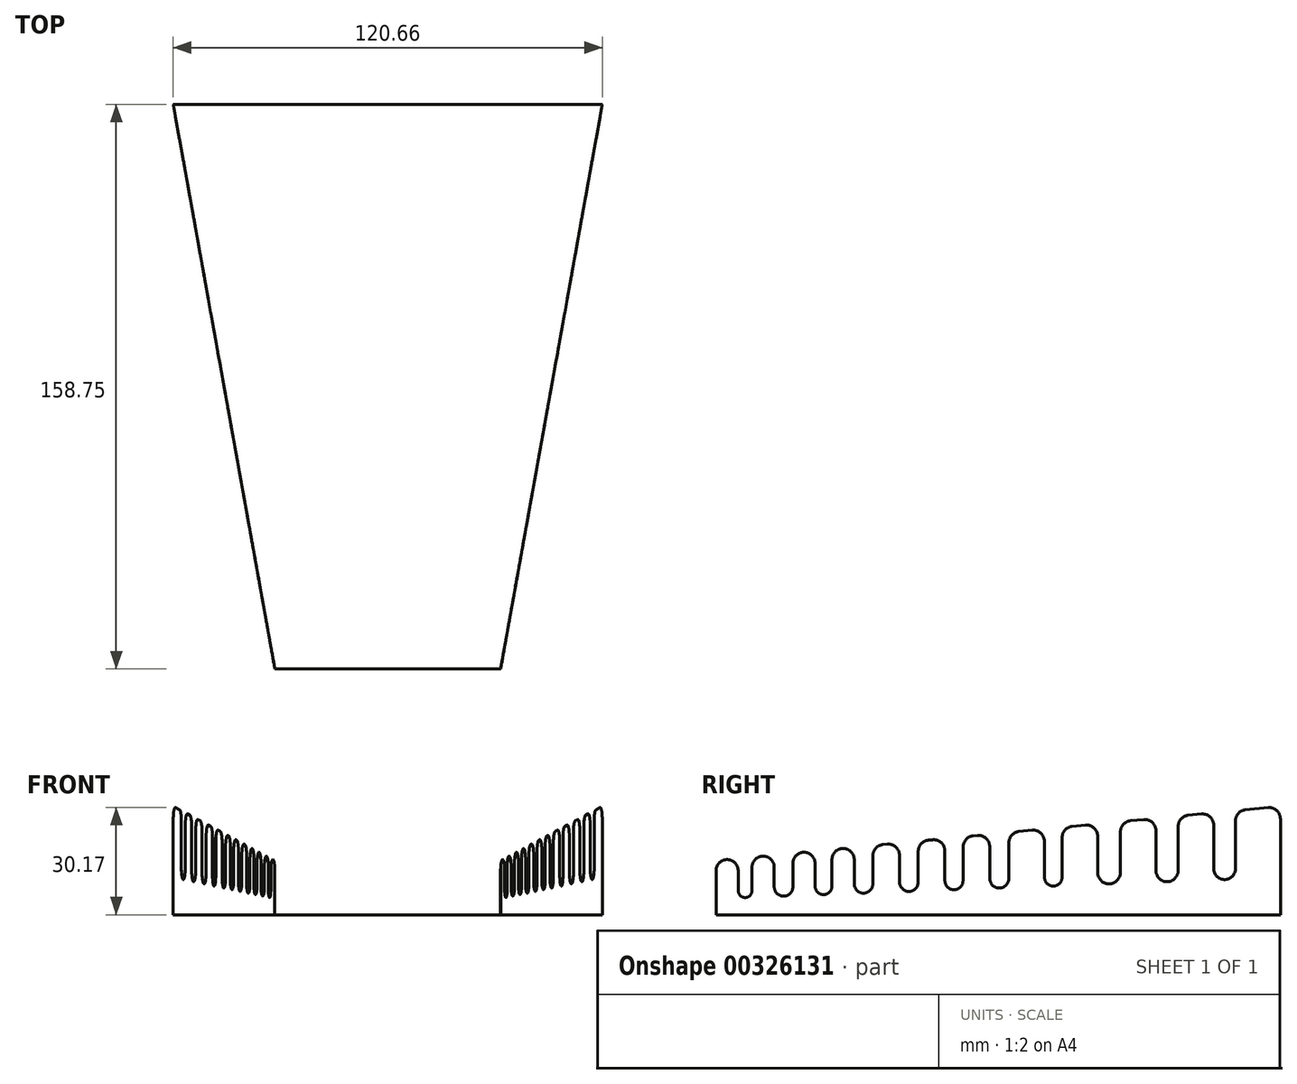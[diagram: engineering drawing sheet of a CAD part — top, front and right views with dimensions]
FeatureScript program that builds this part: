
annotation { "Feature Type Name" : "Feature", "Feature Type Description" : "" }
export const myFeature = defineFeature(function(context is Context, id is Id, definition is map)
    precondition{}
    {
        {
            var Q0;
            Q0=qCreatedBy(makeId("Top.planeOp"),FACE);
            var sketch = newSketch(context, id + "F0", { "sketchPlane" : qUnion([Q0])});
            skLineSegment(sketch, "E0", {"start": v(-31.75, 0) * mm, "end": v(31.75, 0) * mm});
            skLineSegment(sketch, "E1", {"start": v(31.75, 0) * mm, "end": v(60.32, 158.75) * mm});
            skLineSegment(sketch, "E2", {"start": v(60.33, 158.75) * mm, "end": v(-60.33, 158.75) * mm});
            skLineSegment(sketch, "E3", {"start": v(-60.32, 158.75) * mm, "end": v(-31.75, 0) * mm});
            skLineSegment(sketch, "E4", {"start": v(0, 0) * mm, "end": v(0, 306.2) * mm, "construction": true});
            skSolve(sketch);
        }
        {
            var Q0;
            Q0 = qSketchRegion(id + "F0", true);
            extrude(context, id + "F1", {"entities" : qUnion([Q0]), "depth" : 3 / 406.4 * mm});
        }
        {
            var Q0;
            Q0=makeQuery(id+"F1.opExtrude","SWEPT_FACE",FACE,{"disambiguationData":[OSD([sQuery(id+"F0.wireOp",EDGE,"E1")])]});
            var sketch = newSketch(context, id + "F2", { "sketchPlane" : qUnion([Q0])});
            skLineSegment(sketch, "E5", {"start": v(5.62, 0) * mm, "end": v(166.93, 0) * mm});
            skLineSegment(sketch, "E6", {"start": v(166.93, 0) * mm, "end": v(166.93, 27) * mm});
            skLineSegment(sketch, "E7", {"start": v(163.45, 30.15) * mm, "end": v(156.96, 29.54) * mm});
            skLineSegment(sketch, "E8", {"start": v(5.62, 12.35) * mm, "end": v(5.62, 0) * mm});
            skLineSegment(sketch, "E9", {"start": v(104.56, 21.7) * mm, "end": v(104.56, 10.63) * mm});
            skLineSegment(sketch, "E10", {"start": v(99.48, 20.62) * mm, "end": v(99.48, 10.63) * mm});
            skLineSegment(sketch, "E11", {"start": v(89.32, 20.26) * mm, "end": v(89.32, 10.25) * mm});
            skLineSegment(sketch, "E12", {"start": v(83.86, 19.14) * mm, "end": v(83.86, 10.25) * mm});
            skLineSegment(sketch, "E13", {"start": v(76.24, 19.02) * mm, "end": v(76.24, 9.64) * mm});
            skLineSegment(sketch, "E14", {"start": v(71.03, 17.93) * mm, "end": v(71.03, 9.64) * mm});
            skLineSegment(sketch, "E15", {"start": v(63.4, 17.81) * mm, "end": v(63.4, 9.23) * mm});
            skLineSegment(sketch, "E16", {"start": v(58.08, 16.7) * mm, "end": v(58.08, 9.23) * mm});
            skLineSegment(sketch, "E17", {"start": v(38.77, 15.48) * mm, "end": v(38.77, 8.07) * mm});
            skLineSegment(sketch, "E18", {"start": v(33.95, 14.43) * mm, "end": v(33.95, 8.07) * mm});
            skLineSegment(sketch, "E19", {"start": v(27.6, 14.43) * mm, "end": v(27.6, 7.9) * mm});
            skLineSegment(sketch, "E20.trimOffspring", {"start": v(96, 23.78) * mm, "end": v(92.2, 23.42) * mm});
            skLineSegment(sketch, "E21.trimOffspring", {"start": v(80.38, 22.3) * mm, "end": v(79.11, 22.18) * mm});
            skLineSegment(sketch, "E22.trimOffspring", {"start": v(67.56, 21.1) * mm, "end": v(66.29, 20.97) * mm});
            skLineSegment(sketch, "E23.trimOffspring", {"start": v(54.6, 19.87) * mm, "end": v(53.33, 19.75) * mm});
            skLineSegment(sketch, "E24.trimOffspring", {"start": v(30.47, 17.59) * mm, "end": v(30.47, 17.59) * mm});
            skLineSegment(sketch, "E25", {"start": v(22.26, 13.32) * mm, "end": v(22.26, 7.9) * mm});
            skLineSegment(sketch, "E26", {"start": v(15.91, 6.8) * mm, "end": v(15.91, 13.32) * mm});
            skLineSegment(sketch, "E27", {"start": v(11.97, 12.35) * mm, "end": v(11.97, 6.8) * mm});
            skLineSegment(sketch, "E28", {"start": v(45.12, 8.75) * mm, "end": v(45.12, 15.48) * mm});
            skLineSegment(sketch, "E29", {"start": v(50.46, 16.59) * mm, "end": v(50.46, 8.75) * mm});
            skLineSegment(sketch, "E30.trimOffspring", {"start": v(8.5, 15.51) * mm, "end": v(8.5, 15.51) * mm});
            skLineSegment(sketch, "E31.trimOffspring", {"start": v(18.79, 16.48) * mm, "end": v(18.79, 16.48) * mm});
            skLineSegment(sketch, "E32.trimOffspring", {"start": v(41.65, 18.64) * mm, "end": v(41.65, 18.64) * mm});
            skPoint(sketch, "E33.visualSharp", {"position": v(5.62, 15.24) * mm});
            skArc(sketch, "E33.filletArc", {"start": v(8.5, 15.51) * mm, "mid": v(6.45, 14.49) * mm, "end": v(5.62, 12.35) * mm});
            skPoint(sketch, "E34.visualSharp", {"position": v(11.97, 15.84) * mm});
            skArc(sketch, "E34.filletArc", {"start": v(11.97, 12.35) * mm, "mid": v(10.94, 14.7) * mm, "end": v(8.5, 15.51) * mm});
            skPoint(sketch, "E35.visualSharp", {"position": v(15.91, 16.21) * mm});
            skArc(sketch, "E35.filletArc", {"start": v(18.79, 16.48) * mm, "mid": v(16.74, 15.46) * mm, "end": v(15.91, 13.32) * mm});
            skPoint(sketch, "E36.visualSharp", {"position": v(22.26, 16.81) * mm});
            skArc(sketch, "E36.filletArc", {"start": v(22.26, 13.32) * mm, "mid": v(21.22, 15.67) * mm, "end": v(18.79, 16.48) * mm});
            skPoint(sketch, "E37.visualSharp", {"position": v(27.6, 17.32) * mm});
            skArc(sketch, "E37.filletArc", {"start": v(30.47, 17.59) * mm, "mid": v(28.42, 16.56) * mm, "end": v(27.6, 14.43) * mm});
            skPoint(sketch, "E38.visualSharp", {"position": v(33.95, 17.92) * mm});
            skArc(sketch, "E38.filletArc", {"start": v(33.95, 14.43) * mm, "mid": v(32.9, 16.77) * mm, "end": v(30.47, 17.59) * mm});
            skPoint(sketch, "E39.visualSharp", {"position": v(38.77, 18.37) * mm});
            skArc(sketch, "E39.filletArc", {"start": v(41.65, 18.64) * mm, "mid": v(39.6, 17.62) * mm, "end": v(38.77, 15.48) * mm});
            skPoint(sketch, "E40.visualSharp", {"position": v(45.12, 18.97) * mm});
            skArc(sketch, "E40.filletArc", {"start": v(45.12, 15.48) * mm, "mid": v(44.08, 17.83) * mm, "end": v(41.65, 18.64) * mm});
            skPoint(sketch, "E41.visualSharp", {"position": v(50.46, 19.48) * mm});
            skArc(sketch, "E41.filletArc", {"start": v(53.33, 19.75) * mm, "mid": v(51.28, 18.72) * mm, "end": v(50.46, 16.59) * mm});
            skPoint(sketch, "E42.visualSharp", {"position": v(58.08, 20.2) * mm});
            skArc(sketch, "E42.filletArc", {"start": v(58.08, 16.7) * mm, "mid": v(57.04, 19.05) * mm, "end": v(54.6, 19.87) * mm});
            skPoint(sketch, "E43.visualSharp", {"position": v(63.4, 20.7) * mm});
            skArc(sketch, "E43.filletArc", {"start": v(66.29, 20.97) * mm, "mid": v(64.24, 19.95) * mm, "end": v(63.4, 17.81) * mm});
            skPoint(sketch, "E44.visualSharp", {"position": v(71.03, 21.42) * mm});
            skArc(sketch, "E44.filletArc", {"start": v(71.03, 17.93) * mm, "mid": v(70, 20.28) * mm, "end": v(67.56, 21.1) * mm});
            skPoint(sketch, "E45.visualSharp", {"position": v(76.24, 21.91) * mm});
            skArc(sketch, "E45.filletArc", {"start": v(79.11, 22.18) * mm, "mid": v(77.06, 21.16) * mm, "end": v(76.24, 19.02) * mm});
            skPoint(sketch, "E46.visualSharp", {"position": v(83.86, 22.63) * mm});
            skArc(sketch, "E46.filletArc", {"start": v(83.86, 19.14) * mm, "mid": v(82.82, 21.5) * mm, "end": v(80.38, 22.3) * mm});
            skPoint(sketch, "E47.visualSharp", {"position": v(89.32, 23.15) * mm});
            skArc(sketch, "E47.filletArc", {"start": v(92.2, 23.42) * mm, "mid": v(90.14, 22.4) * mm, "end": v(89.32, 20.26) * mm});
            skPoint(sketch, "E48.visualSharp", {"position": v(99.48, 24.1) * mm});
            skArc(sketch, "E48.filletArc", {"start": v(99.48, 20.62) * mm, "mid": v(98.44, 22.97) * mm, "end": v(96, 23.78) * mm});
            skPoint(sketch, "E49.visualSharp", {"position": v(104.56, 24.59) * mm});
            skArc(sketch, "E49.filletArc", {"start": v(107.43, 24.86) * mm, "mid": v(105.38, 23.84) * mm, "end": v(104.56, 21.7) * mm});
            skPoint(sketch, "E50.visualSharp", {"position": v(166.93, 30.48) * mm});
            skArc(sketch, "E50.filletArc", {"start": v(166.93, 27) * mm, "mid": v(165.89, 29.34) * mm, "end": v(163.45, 30.15) * mm});
            skLineSegment(sketch, "E51", {"start": v(14.02, 4.83) * mm, "end": v(151.1, 9.9) * mm, "construction": true});
            skArc(sketch, "E52", {"start": v(11.97, 6.8) * mm, "mid": v(13.94, 4.82) * mm, "end": v(15.91, 6.8) * mm});
            skArc(sketch, "E53", {"start": v(22.26, 7.9) * mm, "mid": v(24.93, 5.23) * mm, "end": v(27.6, 7.9) * mm});
            skArc(sketch, "E54", {"start": v(33.95, 8.07) * mm, "mid": v(36.36, 5.66) * mm, "end": v(38.77, 8.07) * mm});
            skArc(sketch, "E55", {"start": v(45.12, 8.75) * mm, "mid": v(47.79, 6.08) * mm, "end": v(50.46, 8.75) * mm});
            skArc(sketch, "E56", {"start": v(58.08, 9.23) * mm, "mid": v(60.74, 6.56) * mm, "end": v(63.4, 9.23) * mm});
            skArc(sketch, "E57", {"start": v(71.03, 9.64) * mm, "mid": v(73.63, 7.04) * mm, "end": v(76.24, 9.64) * mm});
            skArc(sketch, "E58", {"start": v(83.86, 10.25) * mm, "mid": v(86.59, 7.52) * mm, "end": v(89.32, 10.25) * mm});
            skArc(sketch, "E59", {"start": v(99.48, 10.63) * mm, "mid": v(102.02, 8.09) * mm, "end": v(104.56, 10.63) * mm});
            skLineSegment(sketch, "E60", {"start": v(114.72, 22.06) * mm, "end": v(114.72, 11.92) * mm});
            skLineSegment(sketch, "E61", {"start": v(121.2, 23.27) * mm, "end": v(121.2, 11.92) * mm});
            skLineSegment(sketch, "E62", {"start": v(131.35, 23.63) * mm, "end": v(131.35, 12.47) * mm});
            skLineSegment(sketch, "E63", {"start": v(137.7, 24.83) * mm, "end": v(137.7, 12.47) * mm});
            skLineSegment(sketch, "E64", {"start": v(147.86, 25.19) * mm, "end": v(147.86, 13.02) * mm});
            skLineSegment(sketch, "E65", {"start": v(154.09, 26.38) * mm, "end": v(154.09, 13.02) * mm});
            skArc(sketch, "E66", {"start": v(114.72, 11.92) * mm, "mid": v(117.96, 8.68) * mm, "end": v(121.2, 11.92) * mm});
            skArc(sketch, "E67", {"start": v(131.35, 12.47) * mm, "mid": v(134.53, 9.3) * mm, "end": v(137.7, 12.47) * mm});
            skArc(sketch, "E68", {"start": v(147.86, 13.02) * mm, "mid": v(150.98, 9.9) * mm, "end": v(154.09, 13.02) * mm});
            skLineSegment(sketch, "E69.trimOffspring", {"start": v(144.4, 28.35) * mm, "end": v(140.58, 28) * mm});
            skLineSegment(sketch, "E70.trimOffspring", {"start": v(127.88, 26.8) * mm, "end": v(124.07, 26.43) * mm});
            skLineSegment(sketch, "E71.trimOffspring", {"start": v(111.24, 25.22) * mm, "end": v(107.43, 24.86) * mm});
            skPoint(sketch, "E72.visualSharp", {"position": v(154.09, 29.27) * mm});
            skArc(sketch, "E72.filletArc", {"start": v(156.96, 29.54) * mm, "mid": v(154.91, 28.51) * mm, "end": v(154.09, 26.38) * mm});
            skPoint(sketch, "E73.visualSharp", {"position": v(147.86, 28.68) * mm});
            skArc(sketch, "E73.filletArc", {"start": v(147.86, 25.19) * mm, "mid": v(146.83, 27.54) * mm, "end": v(144.4, 28.35) * mm});
            skPoint(sketch, "E74.visualSharp", {"position": v(137.7, 27.72) * mm});
            skArc(sketch, "E74.filletArc", {"start": v(140.58, 28) * mm, "mid": v(138.53, 26.97) * mm, "end": v(137.7, 24.83) * mm});
            skPoint(sketch, "E75.visualSharp", {"position": v(131.35, 27.12) * mm});
            skArc(sketch, "E75.filletArc", {"start": v(131.35, 23.63) * mm, "mid": v(130.32, 25.98) * mm, "end": v(127.88, 26.8) * mm});
            skPoint(sketch, "E76.visualSharp", {"position": v(121.2, 26.16) * mm});
            skArc(sketch, "E76.filletArc", {"start": v(124.07, 26.43) * mm, "mid": v(122.02, 25.4) * mm, "end": v(121.2, 23.27) * mm});
            skPoint(sketch, "E77.visualSharp", {"position": v(114.72, 25.55) * mm});
            skArc(sketch, "E77.filletArc", {"start": v(114.72, 22.06) * mm, "mid": v(113.68, 24.4) * mm, "end": v(111.24, 25.22) * mm});
            skSolve(sketch);
        }
        {
            var Q0;
            Q0 = qSketchRegion(id + "F2", true);
            extrude(context, id + "F3", {"entities" : qUnion([Q0]), "depth" : 3 / 406.4 * mm});
        }
        {
            var Q0;
            Q0=makeQuery(id+"F3.opExtrude","SWEPT_BODY",BODY,{"disambiguationData":[OSD([sQuery(id+"F2.wireOp",EDGE,"E5"),sQuery(id+"F2.wireOp",EDGE,"E6"),sQuery(id+"F2.wireOp",EDGE,"E7"),sQuery(id+"F2.wireOp",EDGE,"E8"),sQuery(id+"F2.wireOp",EDGE,"E9"),sQuery(id+"F2.wireOp",EDGE,"E10"),sQuery(id+"F2.wireOp",EDGE,"E11"),sQuery(id+"F2.wireOp",EDGE,"E12"),sQuery(id+"F2.wireOp",EDGE,"E13"),sQuery(id+"F2.wireOp",EDGE,"E14"),sQuery(id+"F2.wireOp",EDGE,"E15"),sQuery(id+"F2.wireOp",EDGE,"E16"),sQuery(id+"F2.wireOp",EDGE,"E17"),sQuery(id+"F2.wireOp",EDGE,"E18"),sQuery(id+"F2.wireOp",EDGE,"E19"),sQuery(id+"F2.wireOp",EDGE,"E20.trimOffspring"),sQuery(id+"F2.wireOp",EDGE,"E21.trimOffspring"),sQuery(id+"F2.wireOp",EDGE,"E22.trimOffspring"),sQuery(id+"F2.wireOp",EDGE,"E23.trimOffspring"),sQuery(id+"F2.wireOp",EDGE,"E24.trimOffspring"),sQuery(id+"F2.wireOp",EDGE,"E25"),sQuery(id+"F2.wireOp",EDGE,"E26"),sQuery(id+"F2.wireOp",EDGE,"E27"),sQuery(id+"F2.wireOp",EDGE,"E28"),sQuery(id+"F2.wireOp",EDGE,"E29"),sQuery(id+"F2.wireOp",EDGE,"E30.trimOffspring"),sQuery(id+"F2.wireOp",EDGE,"E31.trimOffspring"),sQuery(id+"F2.wireOp",EDGE,"E32.trimOffspring"),sQuery(id+"F2.wireOp",EDGE,"44bdaeef-af40-4c73-8f6e-6d99c36835f4.filletArc"),sQuery(id+"F2.wireOp",EDGE,"6b3ca2c0-dadf-406b-9eff-c9a17f8ad7e2.filletArc"),sQuery(id+"F2.wireOp",EDGE,"1fa86d9b-671f-451e-833e-d4d190dc1f45.filletArc"),sQuery(id+"F2.wireOp",EDGE,"3b8eb195-600f-4a37-b847-6e8cf2265463.filletArc"),sQuery(id+"F2.wireOp",EDGE,"bc049c84-9569-4731-b49c-76ca646e6f82.filletArc"),sQuery(id+"F2.wireOp",EDGE,"77aef3f9-ae1d-4147-bc1f-e498b1b49d45.filletArc"),sQuery(id+"F2.wireOp",EDGE,"ad07f970-fb9d-4c7d-af48-0ce4067abd56.filletArc"),sQuery(id+"F2.wireOp",EDGE,"9913eee0-3d8a-4413-986c-34ea99986887.filletArc"),sQuery(id+"F2.wireOp",EDGE,"c9ab13b8-8898-4061-a878-8181e42116e4.filletArc"),sQuery(id+"F2.wireOp",EDGE,"b0b1a9dd-5b3d-403a-bff8-4318d5c8f1fc.filletArc"),sQuery(id+"F2.wireOp",EDGE,"1ffb475e-37b7-4818-bbfe-a6cc4202deda.filletArc"),sQuery(id+"F2.wireOp",EDGE,"68e06a09-0fdf-4d65-9fec-2a2e093ea59b.filletArc"),sQuery(id+"F2.wireOp",EDGE,"77b9f98a-97c3-4de9-a10d-d998596987cd.filletArc"),sQuery(id+"F2.wireOp",EDGE,"719c6fb4-1f70-42a9-9ee2-d1cfad0e4618.filletArc"),sQuery(id+"F2.wireOp",EDGE,"f5dae8e6-8fe6-4f3b-b72b-1b05ff77a15d.filletArc"),sQuery(id+"F2.wireOp",EDGE,"b93fcb5e-d222-4fd1-a0e3-2853195c284a.filletArc"),sQuery(id+"F2.wireOp",EDGE,"E33.filletArc"),sQuery(id+"F2.wireOp",EDGE,"E34.filletArc"),sQuery(id+"F2.wireOp",EDGE,"E35.filletArc"),sQuery(id+"F2.wireOp",EDGE,"E36.filletArc"),sQuery(id+"F2.wireOp",EDGE,"E37.filletArc"),sQuery(id+"F2.wireOp",EDGE,"E38.filletArc"),sQuery(id+"F2.wireOp",EDGE,"E39.filletArc"),sQuery(id+"F2.wireOp",EDGE,"E40.filletArc"),sQuery(id+"F2.wireOp",EDGE,"E41.filletArc"),sQuery(id+"F2.wireOp",EDGE,"E42.filletArc"),sQuery(id+"F2.wireOp",EDGE,"E43.filletArc"),sQuery(id+"F2.wireOp",EDGE,"E44.filletArc"),sQuery(id+"F2.wireOp",EDGE,"E45.filletArc"),sQuery(id+"F2.wireOp",EDGE,"E46.filletArc"),sQuery(id+"F2.wireOp",EDGE,"E47.filletArc"),sQuery(id+"F2.wireOp",EDGE,"E48.filletArc"),sQuery(id+"F2.wireOp",EDGE,"E49.filletArc"),sQuery(id+"F2.wireOp",EDGE,"E50.filletArc")])]});
            var Q1;
            Q1=qCreatedBy(makeId("Right.planeOp"),FACE);
            mirror(context, id + "F4", {"entities" : qUnion([Q0]), "mirrorPlane" : qUnion([Q1])});
        }
    });
